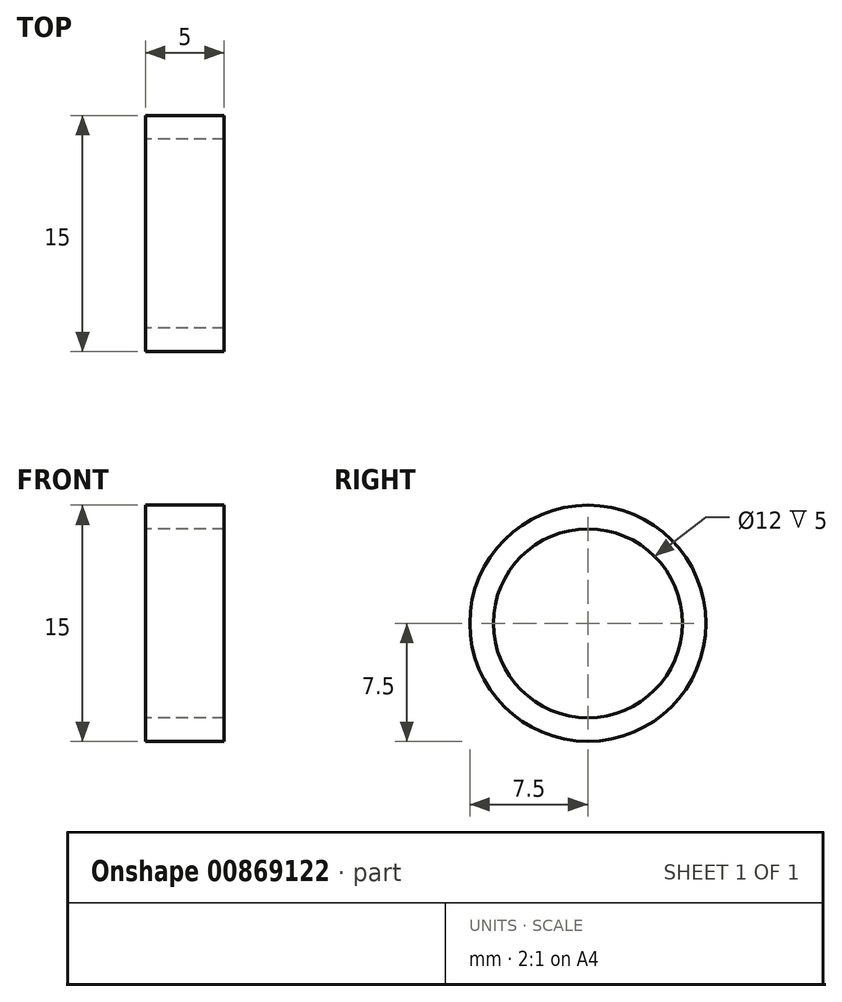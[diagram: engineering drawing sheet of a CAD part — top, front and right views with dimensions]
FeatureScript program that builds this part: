
annotation { "Feature Type Name" : "Feature", "Feature Type Description" : "" }
export const myFeature = defineFeature(function(context is Context, id is Id, definition is map)
    precondition{}
    {
        {
            var Q0;
            Q0=qCreatedBy(makeId("Right.planeOp"),FACE);
            var sketch = newSketch(context, id + "F0", { "sketchPlane" : qUnion([Q0]), "disableImprinting" : false});
            skCircle(sketch, "E0", {"center": v(0, 0) * mm, "radius": 7.5 * mm});
            skCircle(sketch, "E1", {"center": v(0, 0) * mm, "radius": 6 * mm});
            skSolve(sketch);
        }
        {
            var Q0;
            Q0 = qSketchRegion(id + "F0", true);
            extrude(context, id + "F1", {"entities" : qUnion([Q0]), "flatOperationType" : FlatOperationType.REMOVE, "depth" : 5 * mm, "offsetDistance" : 25 * mm, "startOffsetBound" : StartOffsetType.BLIND, "startOffsetDistance" : 25 * mm, "symmetric" : true, "domain" : OperationDomain.MODEL});
        }
    });
